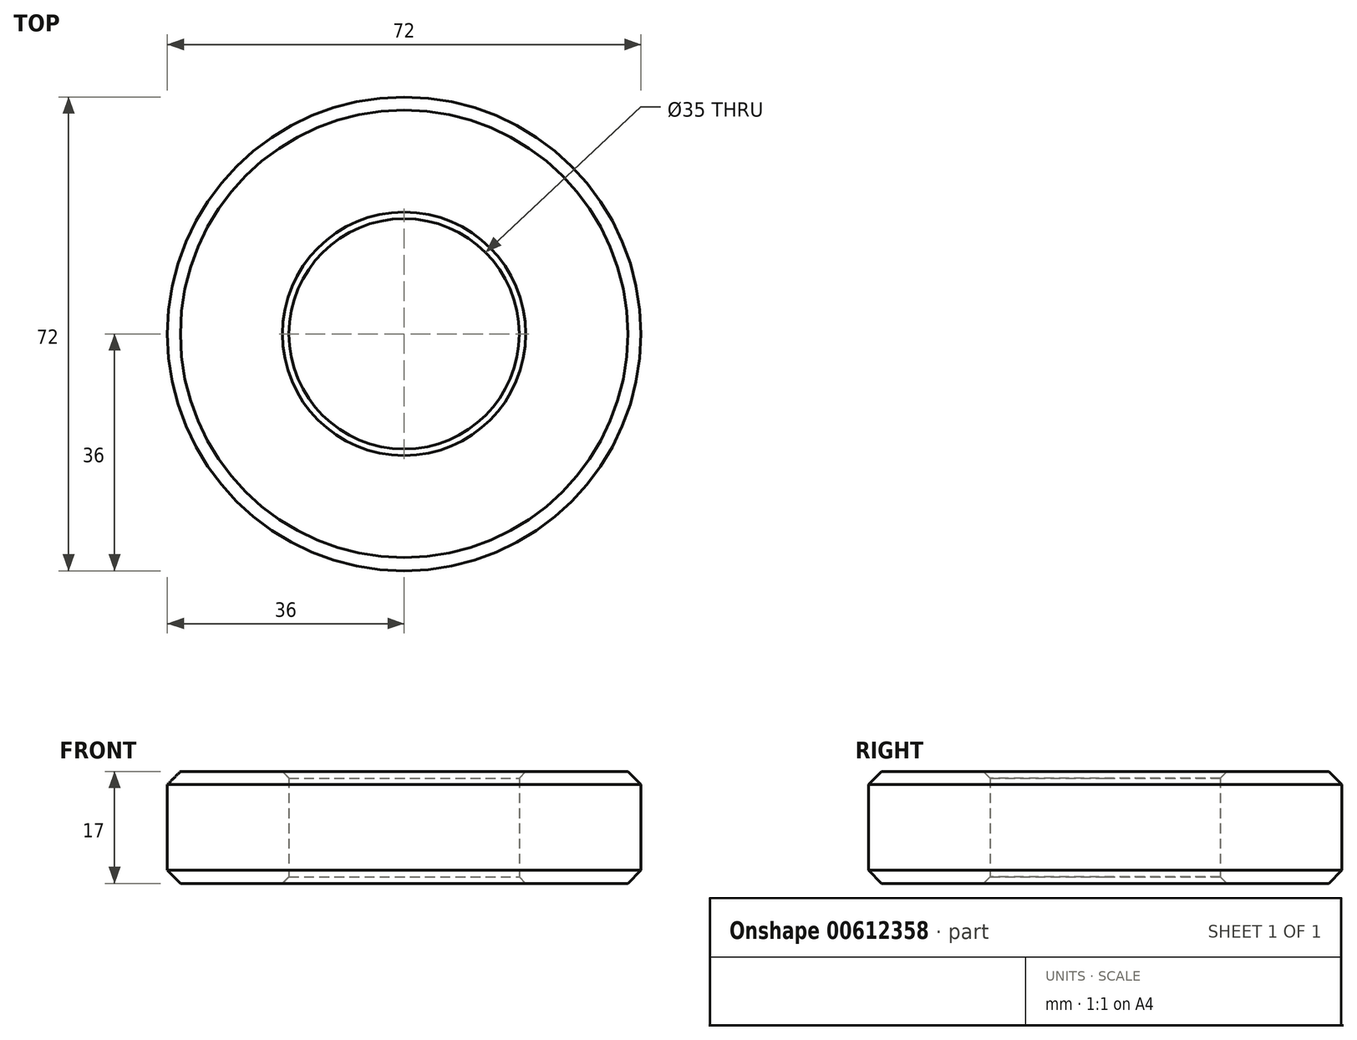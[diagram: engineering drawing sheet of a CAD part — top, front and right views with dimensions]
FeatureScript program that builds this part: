
annotation { "Feature Type Name" : "Feature", "Feature Type Description" : "" }
export const myFeature = defineFeature(function(context is Context, id is Id, definition is map)
    precondition{}
    {
        {
            var Q0;
            Q0=qCreatedBy(makeId("Front.planeOp"),FACE);
            var sketch = newSketch(context, id + "F0", { "sketchPlane" : qUnion([Q0])});
            skLineSegment(sketch, "E0", {"start": v(0, 0) * mm, "end": v(0, 14.58) * mm});
            skLineSegment(sketch, "E1.bottom", {"start": v(17.5, 0) * mm, "end": v(36, 0) * mm});
            skLineSegment(sketch, "E1.top", {"start": v(17.5, 17) * mm, "end": v(36, 17) * mm});
            skLineSegment(sketch, "E1.left", {"start": v(17.5, 0) * mm, "end": v(17.5, 17) * mm});
            skLineSegment(sketch, "E1.right", {"start": v(36, 0) * mm, "end": v(36, 17) * mm});
            skSolve(sketch);
        }
        {
            var Q0;
            Q0=makeQuery(id+"F0.imprint","IMPRINT",FACE,{"disambiguationData":[TD([[makeQuery(id+"F0.imprint","IMPRINT",EDGE,{"derivedFrom":sQuery(id+"F0.wireOp",EDGE,"E1.bottom")}),1.0]])]});
            var Q1;
            Q1=sQuery(id+"F0.wireOp",EDGE,"E0");
            revolve(context, id + "F1", {"entities" : qUnion([Q0]), "axis" : qUnion([Q1]), "revolveType" : RevolveType.FULL});
        }
        {
            var Q0;
            Q0=makeQuery(id+"F1.opRevolve","SWEPT_EDGE",EDGE,{"disambiguationData":[OSD([sQuery(id+"F0.wireOp",EDGE,"E1.top"),sQuery(id+"F0.wireOp",EDGE,"E1.right")])]});
            var Q1;
            Q1=makeQuery(id+"F1.opRevolve","SWEPT_FACE",FACE,{"disambiguationData":[OSD([sQuery(id+"F0.wireOp",EDGE,"E1.right")])]});
            chamfer(context, id + "F2", {"entities" : qUnion([Q0, Q1]), "width" : 2 * mm, "tangentPropagation" : true});
        }
        {
            var Q0;
            Q0=makeQuery(id+"F1.opRevolve","SWEPT_EDGE",EDGE,{"disambiguationData":[OSD([sQuery(id+"F0.wireOp",EDGE,"E1.top"),sQuery(id+"F0.wireOp",EDGE,"E1.left")])]});
            var Q1;
            Q1=makeQuery(id+"F1.opRevolve","SWEPT_EDGE",EDGE,{"disambiguationData":[OSD([sQuery(id+"F0.wireOp",EDGE,"E1.bottom"),sQuery(id+"F0.wireOp",EDGE,"E1.left")])]});
            chamfer(context, id + "F3", {"entities" : qUnion([Q0, Q1]), "width" : 1 * mm, "tangentPropagation" : true});
        }
    });
